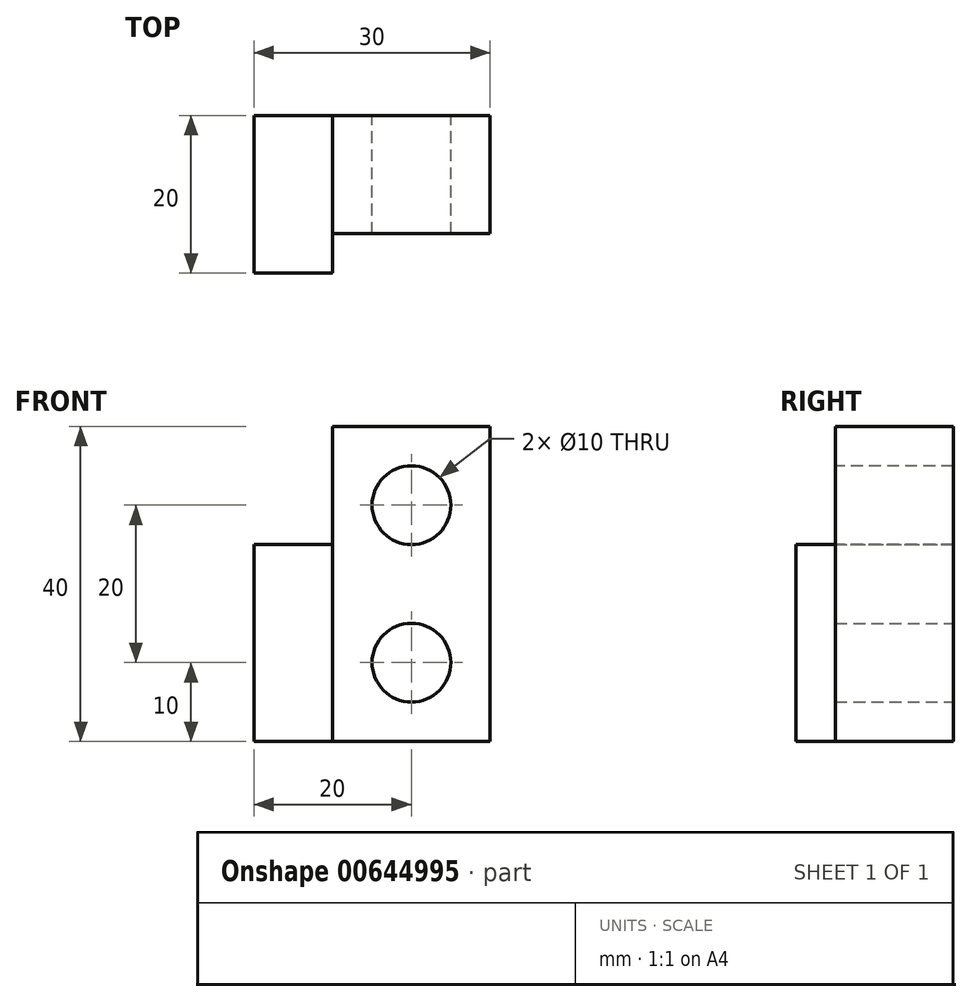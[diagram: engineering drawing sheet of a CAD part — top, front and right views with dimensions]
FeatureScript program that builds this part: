
annotation { "Feature Type Name" : "Feature", "Feature Type Description" : "" }
export const myFeature = defineFeature(function(context is Context, id is Id, definition is map)
    precondition{}
    {
        {
            var Q0;
            Q0=qCreatedBy(makeId("Front.planeOp"),FACE);
            var sketch = newSketch(context, id + "F0", { "sketchPlane" : qUnion([Q0])});
            skLineSegment(sketch, "E0.bottom", {"start": v(-10, 20) * mm, "end": v(10, 20) * mm});
            skLineSegment(sketch, "E0.top", {"start": v(-10, -20) * mm, "end": v(10, -20) * mm});
            skLineSegment(sketch, "E0.left", {"start": v(-10, 20) * mm, "end": v(-10, -20) * mm});
            skLineSegment(sketch, "E0.right", {"start": v(10, 20) * mm, "end": v(10, -20) * mm});
            skPoint(sketch, "E0.middle", {"position": v(0, 0) * mm});
            skLineSegment(sketch, "E1.left", {"start": v(-10, -20) * mm, "end": v(-10, 10.71) * mm});
            skLineSegment(sketch, "E2.bottom", {"start": v(-10, -20) * mm, "end": v(-20, -20) * mm});
            skLineSegment(sketch, "E2.top", {"start": v(-10, 5) * mm, "end": v(-20, 5) * mm});
            skLineSegment(sketch, "E2.left", {"start": v(-10, -20) * mm, "end": v(-10, 5) * mm});
            skLineSegment(sketch, "E2.right", {"start": v(-20, -20) * mm, "end": v(-20, 5) * mm});
            skCircle(sketch, "E3", {"center": v(0, -10) * mm, "radius": 5 * mm});
            skSolve(sketch);
        }
        {
            var Q0;
            Q0=makeQuery(id+"F0.imprint","IMPRINT",FACE,{"disambiguationData":[TD([[makeQuery(id+"F0.imprint","IMPRINT",EDGE,{"derivedFrom":sQuery(id+"F0.wireOp",EDGE,"E0.bottom")}),-1.0]])]});
            extrude(context, id + "F1", {"entities" : qUnion([Q0]), "depth" : 15 * mm, "offsetDistance" : 25 * mm});
        }
        {
            var Q0;
            Q0=makeQuery(id+"F0.imprint","IMPRINT",FACE,{"disambiguationData":[TD([[makeQuery(id+"F0.imprint","IMPRINT",EDGE,{"derivedFrom":sQuery(id+"F0.wireOp",EDGE,"E2.bottom")}),-1.0]])]});
            extrude(context, id + "F2", {"entities" : qUnion([Q0]), "operationType" : NewBodyOperationType.ADD, "depth" : 20 * mm, "offsetDistance" : 25 * mm});
        }
        {
            var Q0;
            Q0=makeQuery(id+"F1.opExtrude","CAP_FACE",FACE,{"disambiguationData":[OSD([sQuery(id+"F0.wireOp",EDGE,"E0.bottom"),sQuery(id+"F0.wireOp",EDGE,"E0.top"),sQuery(id+"F0.wireOp",EDGE,"E0.left"),sQuery(id+"F0.wireOp",EDGE,"E0.right"),sQuery(id+"F0.wireOp",EDGE,"E1.left"),sQuery(id+"F0.wireOp",EDGE,"E2.left"),sQuery(id+"F0.wireOp",EDGE,"E3")])],"isStart":false});
            var sketch = newSketch(context, id + "F3", { "sketchPlane" : qUnion([Q0])});
            skCircle(sketch, "E4", {"center": v(0, 10) * mm, "radius": 5 * mm});
            skSolve(sketch);
        }
        {
            var Q0;
            Q0=makeQuery(id+"F3.imprint","IMPRINT",FACE,{"disambiguationData":[TD([[makeQuery(id+"F3.imprint","IMPRINT",EDGE,{"derivedFrom":sQuery(id+"F3.wireOp",EDGE,"E4")}),1.0]])]});
            var Q1;
            {var subQ0=sQuery(id+"F0.wireOp",EDGE,"E2.left");Q1=makeQuery(id+"F2.boolean.opBoolean","MERGE",FACE,{"derivedFrom":[makeQuery(id+"F1.opExtrude","CAP_FACE",FACE,{"disambiguationData":[OSD([sQuery(id+"F0.wireOp",EDGE,"E0.bottom"),sQuery(id+"F0.wireOp",EDGE,"E0.top"),sQuery(id+"F0.wireOp",EDGE,"E0.left"),sQuery(id+"F0.wireOp",EDGE,"E0.right"),sQuery(id+"F0.wireOp",EDGE,"E1.left"),subQ0,sQuery(id+"F0.wireOp",EDGE,"E3")])],"isStart":true}),makeQuery(id+"F2.opExtrude","CAP_FACE",FACE,{"disambiguationData":[OSD([sQuery(id+"F0.wireOp",EDGE,"E2.bottom"),sQuery(id+"F0.wireOp",EDGE,"E2.top"),subQ0,sQuery(id+"F0.wireOp",EDGE,"E2.right")])],"isStart":true})]});}
            extrude(context, id + "F4", {"entities" : qUnion([Q0]), "operationType" : NewBodyOperationType.REMOVE, "endBound" : BoundingType.UP_TO_SURFACE, "oppositeDirection" : true, "depth" : 25 * mm, "endBoundEntityFace" : qUnion([Q1]), "offsetDistance" : 25 * mm});
        }
    });
